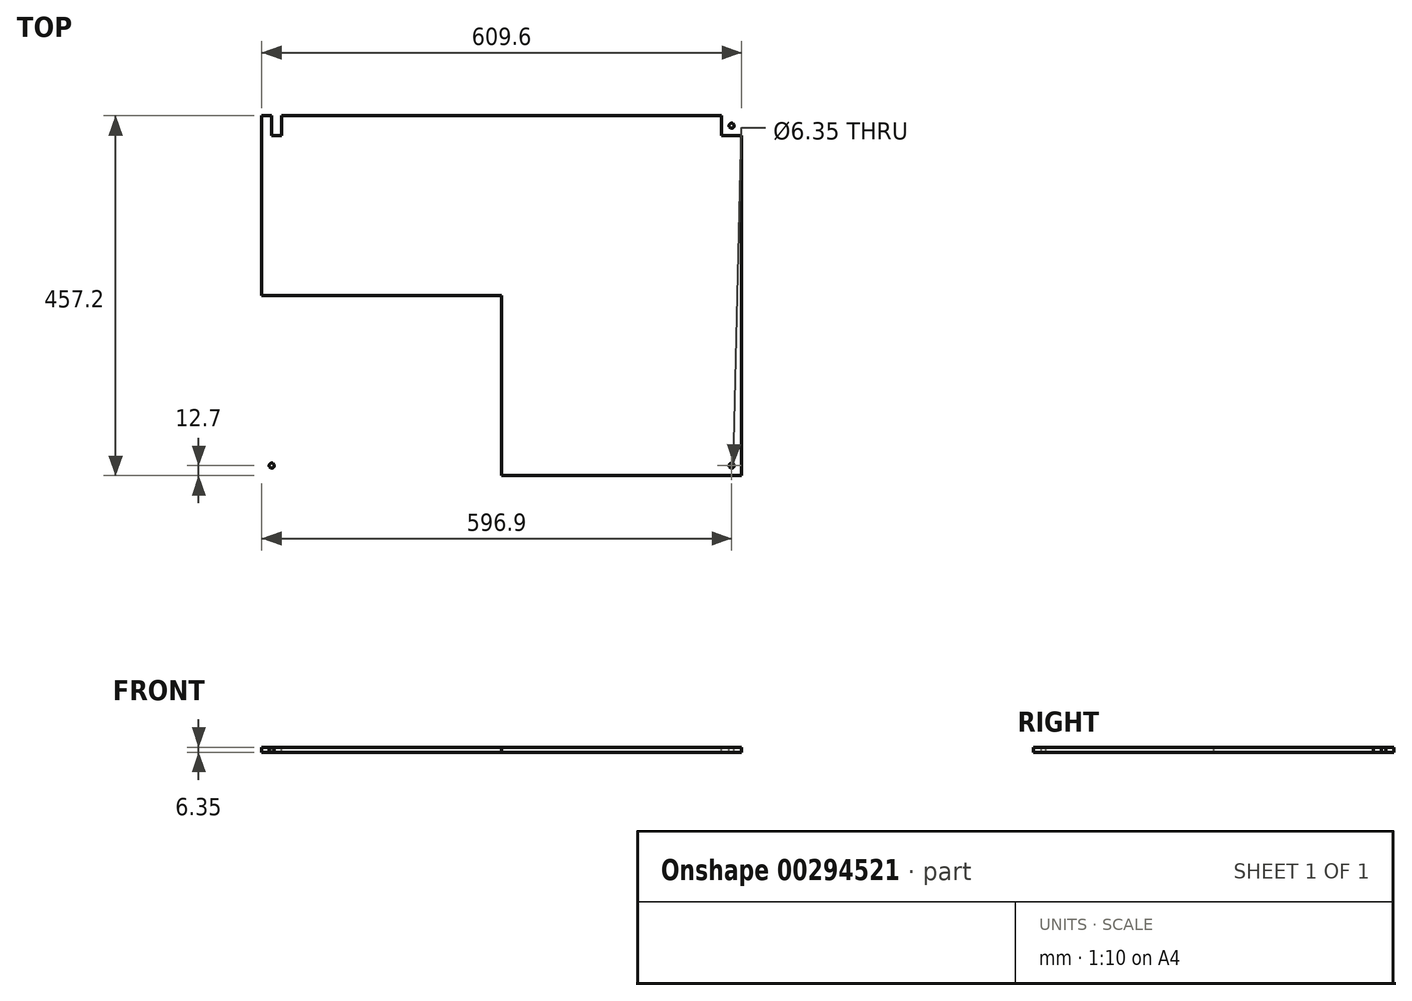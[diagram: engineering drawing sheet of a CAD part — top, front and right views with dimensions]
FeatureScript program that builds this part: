
annotation { "Feature Type Name" : "Feature", "Feature Type Description" : "" }
export const myFeature = defineFeature(function(context is Context, id is Id, definition is map)
    precondition{}
    {
        {
            var Q0;
            Q0=qCreatedBy(makeId("Top.planeOp"),FACE);
            var sketch = newSketch(context, id + "F0", { "sketchPlane" : qUnion([Q0])});
            skLineSegment(sketch, "E0.bottom", {"start": v(304.8, 228.6) * mm, "end": v(-304.8, 228.6) * mm});
            skLineSegment(sketch, "E0.top", {"start": v(304.8, -228.6) * mm, "end": v(-304.8, -228.6) * mm});
            skLineSegment(sketch, "E0.left", {"start": v(304.8, 228.6) * mm, "end": v(304.8, -228.6) * mm});
            skLineSegment(sketch, "E0.right", {"start": v(-304.8, 228.6) * mm, "end": v(-304.8, -228.6) * mm});
            skPoint(sketch, "E0.middle", {"position": v(0, 0) * mm});
            skSolve(sketch);
        }
        {
            var Q0;
            Q0=makeQuery(id+"F0.imprint","IMPRINT",FACE,{"disambiguationData":[TD([[makeQuery(id+"F0.imprint","IMPRINT",EDGE,{"derivedFrom":sQuery(id+"F0.wireOp",EDGE,"E0.bottom")}),1.0]])]});
            extrude(context, id + "F1", {"entities" : qUnion([Q0]), "depth" : 6.35 * mm});
        }
        {
            var Q0;
            Q0=makeQuery(id+"F1.opExtrude","CAP_FACE",FACE,{"disambiguationData":[OSD([sQuery(id+"F0.wireOp",EDGE,"E0.bottom"),sQuery(id+"F0.wireOp",EDGE,"E0.top"),sQuery(id+"F0.wireOp",EDGE,"E0.left"),sQuery(id+"F0.wireOp",EDGE,"E0.right")])],"isStart":false});
            var sketch = newSketch(context, id + "F2", { "sketchPlane" : qUnion([Q0])});
            skLineSegment(sketch, "E1", {"start": v(-304.8, 0) * mm, "end": v(304.8, 0) * mm});
            skLineSegment(sketch, "E2", {"start": v(0, 228.6) * mm, "end": v(0, -228.6) * mm});
            skLineSegment(sketch, "E3.bottom", {"start": v(-304.8, 228.6) * mm, "end": v(-279.4, 228.6) * mm});
            skLineSegment(sketch, "E3.top", {"start": v(-304.8, 203.2) * mm, "end": v(-279.4, 203.2) * mm});
            skLineSegment(sketch, "E3.left", {"start": v(-304.8, 228.6) * mm, "end": v(-304.8, 203.2) * mm});
            skLineSegment(sketch, "E3.right", {"start": v(-279.4, 228.6) * mm, "end": v(-279.4, 203.2) * mm});
            skLineSegment(sketch, "E4", {"start": v(-304.8, 215.9) * mm, "end": v(-279.4, 215.9) * mm});
            skLineSegment(sketch, "E5", {"start": v(-292.1, 228.6) * mm, "end": v(-292.1, 203.2) * mm});
            skCircle(sketch, "E6", {"center": v(-292.1, 215.9) * mm, "radius": 3.18 * mm});
            skLineSegment(sketch, "E7.MirrorCS", {"start": v(279.4, 228.6) * mm, "end": v(279.4, 203.2) * mm});
            skLineSegment(sketch, "E8.MirrorCS", {"start": v(292.1, 228.6) * mm, "end": v(292.1, 203.2) * mm});
            skCircle(sketch, "E9.MirrorC", {"center": v(292.1, 215.9) * mm, "radius": 3.18 * mm});
            skLineSegment(sketch, "E10.MirrorCS", {"start": v(304.8, 203.2) * mm, "end": v(279.4, 203.2) * mm});
            skCircle(sketch, "E11.MirrorC", {"center": v(-292.1, -215.9) * mm, "radius": 3.18 * mm});
            skCircle(sketch, "E12.MirrorC", {"center": v(292.1, -215.9) * mm, "radius": 3.18 * mm});
            skSolve(sketch);
        }
        {
            var Q0;
            {var subQ0=sQuery(id+"F2.wireOp",EDGE,"E5");var subQ1=sQuery(id+"F2.wireOp",EDGE,"E4");var subQ2=makeQuery(id+"F2.imprint","INTERSECT",VERTEX,{"derivedFrom":[subQ1,subQ0]});Q0=makeQuery(id+"F2.imprint","IMPRINT",FACE,{"disambiguationData":[TD([[makeQuery(id+"F2.imprint","IMPRINT",EDGE,{"disambiguationData":[TD([[subQ2,-1.0]])],"derivedFrom":subQ1}),1.0]])]});}
            var Q1;
            {var subQ0=sQuery(id+"F2.wireOp",EDGE,"E6");var subQ1=sQuery(id+"F2.wireOp",EDGE,"E4");var subQ2=makeQuery(id+"F2.imprint","INTERSECT",VERTEX,{"disambiguationData":[OD(0.0)],"derivedFrom":[subQ1,subQ0]});Q1=makeQuery(id+"F2.imprint","IMPRINT",FACE,{"disambiguationData":[TD([[makeQuery(id+"F2.imprint","IMPRINT",EDGE,{"disambiguationData":[TD([[subQ2,-1.0]])],"derivedFrom":subQ1}),1.0]])]});}
            var Q2;
            {var subQ0=sQuery(id+"F2.wireOp",EDGE,"E6");var subQ1=sQuery(id+"F2.wireOp",EDGE,"E4");var subQ2=makeQuery(id+"F2.imprint","INTERSECT",VERTEX,{"disambiguationData":[OD(0.0)],"derivedFrom":[subQ1,subQ0]});Q2=makeQuery(id+"F2.imprint","IMPRINT",FACE,{"disambiguationData":[TD([[makeQuery(id+"F2.imprint","IMPRINT",EDGE,{"disambiguationData":[TD([[subQ2,-1.0]])],"derivedFrom":subQ1}),-1.0]])]});}
            var Q3;
            {var subQ0=sQuery(id+"F2.wireOp",EDGE,"E5");var subQ1=sQuery(id+"F2.wireOp",EDGE,"E4");var subQ2=makeQuery(id+"F2.imprint","INTERSECT",VERTEX,{"derivedFrom":[subQ1,subQ0]});Q3=makeQuery(id+"F2.imprint","IMPRINT",FACE,{"disambiguationData":[TD([[makeQuery(id+"F2.imprint","IMPRINT",EDGE,{"disambiguationData":[TD([[subQ2,-1.0]])],"derivedFrom":subQ1}),-1.0]])]});}
            var Q4;
            Q4=makeQuery(id+"F2.imprint","IMPRINT",FACE,{"disambiguationData":[TD([[makeQuery(id+"F2.imprint","IMPRINT",EDGE,{"derivedFrom":sQuery(id+"F2.wireOp",EDGE,"E11.MirrorC")}),-1.0]])]});
            var Q5;
            Q5=makeQuery(id+"F2.imprint","IMPRINT",FACE,{"disambiguationData":[TD([[makeQuery(id+"F2.imprint","IMPRINT",EDGE,{"derivedFrom":sQuery(id+"F2.wireOp",EDGE,"E12.MirrorC")}),1.0]])]});
            var Q6;
            {var subQ0=sQuery(id+"F2.wireOp",EDGE,"E9.MirrorC");var subQ1=sQuery(id+"F2.wireOp",EDGE,"E8.MirrorCS");var subQ2=makeQuery(id+"F2.imprint","INTERSECT",VERTEX,{"disambiguationData":[OD(0.0)],"derivedFrom":[subQ1,subQ0]});Q6=makeQuery(id+"F2.imprint","IMPRINT",FACE,{"disambiguationData":[TD([[makeQuery(id+"F2.imprint","IMPRINT",EDGE,{"disambiguationData":[TD([[subQ2,-1.0]])],"derivedFrom":subQ1}),1.0]])]});}
            var Q7;
            {var subQ0=sQuery(id+"F2.wireOp",EDGE,"E9.MirrorC");var subQ1=sQuery(id+"F2.wireOp",EDGE,"E8.MirrorCS");var subQ2=makeQuery(id+"F2.imprint","INTERSECT",VERTEX,{"disambiguationData":[OD(0.0)],"derivedFrom":[subQ1,subQ0]});Q7=makeQuery(id+"F2.imprint","IMPRINT",FACE,{"disambiguationData":[TD([[makeQuery(id+"F2.imprint","IMPRINT",EDGE,{"disambiguationData":[TD([[subQ2,-1.0]])],"derivedFrom":subQ1}),-1.0]])]});}
            extrude(context, id + "F3", {"entities" : qUnion([Q0, Q1, Q2, Q3, Q4, Q5, Q6, Q7]), "operationType" : NewBodyOperationType.REMOVE, "oppositeDirection" : true, "depth" : 6.35 * mm});
        }
    });
